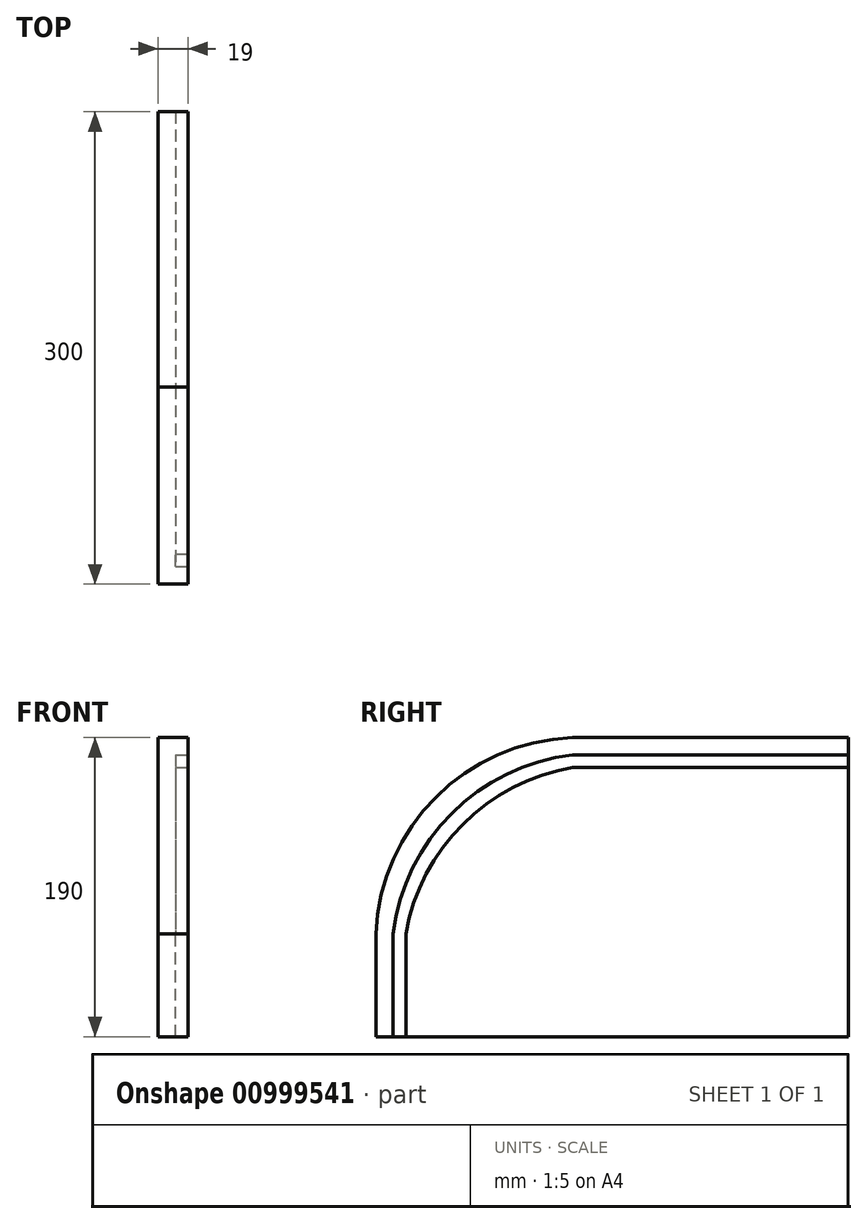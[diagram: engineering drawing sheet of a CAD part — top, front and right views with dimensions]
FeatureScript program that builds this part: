
annotation { "Feature Type Name" : "Feature", "Feature Type Description" : "" }
export const myFeature = defineFeature(function(context is Context, id is Id, definition is map)
    precondition{}
    {
        {
            var Q0;
            Q0=qCreatedBy(makeId("Right.planeOp"),FACE);
            var sketch = newSketch(context, id + "F0", { "sketchPlane" : qUnion([Q0]), "disableImprinting" : false});
            skLineSegment(sketch, "E0.bottom", {"start": v(-25, 95) * mm, "end": v(150, 95) * mm});
            skLineSegment(sketch, "E0.top", {"start": v(-150, -95) * mm, "end": v(150, -95) * mm});
            skLineSegment(sketch, "E0.left", {"start": v(-150, -29.82) * mm, "end": v(-150, -95) * mm});
            skLineSegment(sketch, "E0.right", {"start": v(150, 95) * mm, "end": v(150, -95) * mm});
            skPoint(sketch, "E0.middle", {"position": v(0, 0) * mm});
            skPoint(sketch, "E1", {"position": v(-150, -40) * mm});
            skPoint(sketch, "E2", {"position": v(-25, 95) * mm});
            skArc(sketch, "E3", {"start": v(-25, 95) * mm, "mid": v(-115.49, 53.42) * mm, "end": v(-150, -40) * mm});
            skPoint(sketch, "E4.orphan", {"position": v(-150, 95) * mm});
            skSolve(sketch);
        }
        {
            var Q0;
            {var subQ5=sQuery(id+"F0.wireOp",EDGE,"E0.bottom");Q0=makeQuery(id+"F0.imprint","IMPRINT",FACE,{"disambiguationData":[TD([[makeQuery(id+"F0.imprint","IMPRINT",EDGE,{"derivedFrom":subQ5}),-1.0]])]});}
            extrude(context, id + "F1", {"entities" : qUnion([Q0]), "flatOperationType" : FlatOperationType.REMOVE, "thickness1" : 5 * mm, "thickness2" : 0 * mm, "thickness" : 5 * mm, "depth" : 19 * mm, "offsetDistance" : 25 * mm, "startOffsetBound" : StartOffsetType.BLIND, "startOffsetDistance" : 25 * mm, "domain" : OperationDomain.MODEL});
        }
        {
            var Q0;
            Q0=makeQuery(id+"F1.opExtrude","CAP_FACE",FACE,{"disambiguationData":[OSD([sQuery(id+"F0.wireOp",EDGE,"E0.bottom"),sQuery(id+"F0.wireOp",EDGE,"E0.top"),sQuery(id+"F0.wireOp",EDGE,"E0.left"),sQuery(id+"F0.wireOp",EDGE,"E0.right"),sQuery(id+"F0.wireOp",EDGE,"E3")])],"isStart":false});
            var sketch = newSketch(context, id + "F2", { "sketchPlane" : qUnion([Q0]), "disableImprinting" : false});
            skPoint(sketch, "E5", {"position": v(150, 84) * mm});
            skPoint(sketch, "E6", {"position": v(150, 76) * mm});
            skLineSegment(sketch, "E7", {"start": v(150, 84) * mm, "end": v(-25, 84) * mm});
            skLineSegment(sketch, "E8", {"start": v(150, 76) * mm, "end": v(-25, 76) * mm});
            skPoint(sketch, "E9", {"position": v(-139, -95) * mm});
            skPoint(sketch, "E10", {"position": v(-131, -95) * mm});
            skLineSegment(sketch, "E11", {"start": v(-139, -95) * mm, "end": v(-139, -29.82) * mm});
            skLineSegment(sketch, "E12", {"start": v(-131, -95) * mm, "end": v(-131, -29.82) * mm});
            skArc(sketch, "E13", {"start": v(-25, 76) * mm, "mid": v(-94.77, 39.9) * mm, "end": v(-131, -29.82) * mm});
            skArc(sketch, "E14", {"start": v(-25, 84) * mm, "mid": v(-101.75, 46.88) * mm, "end": v(-139, -29.82) * mm});
            skSolve(sketch);
        }
        {
            var Q0;
            {var subQ1=sQuery(id+"F2.wireOp",EDGE,"E7");Q0=makeQuery(id+"F2.imprint","IMPRINT",FACE,{"disambiguationData":[TD([[makeQuery(id+"F2.imprint","IMPRINT",EDGE,{"derivedFrom":subQ1}),1.0]])]});}
            extrude(context, id + "F3", {"entities" : qUnion([Q0]), "operationType" : NewBodyOperationType.REMOVE, "flatOperationType" : FlatOperationType.REMOVE, "thickness1" : 5 * mm, "thickness2" : 0 * mm, "thickness" : 5 * mm, "oppositeDirection" : true, "depth" : 8 * mm, "offsetDistance" : 25 * mm, "startOffsetBound" : StartOffsetType.BLIND, "startOffsetDistance" : 25 * mm, "domain" : OperationDomain.MODEL});
        }
    });
